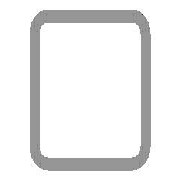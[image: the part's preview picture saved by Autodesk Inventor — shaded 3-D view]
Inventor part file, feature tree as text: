
AUTODESK INVENTOR PART (.ipt)
format: ipt  version: 2025 (Build 290162010, 162A)  size: 134,656 bytes
history: native  units: mm (DEFAULTED — no unit token found)
features: other x4, sketch x1, plane x1
ambient origin geometry x8: Origin, YZ Plane, XZ Plane, XY Plane, X Axis, Y Axis, Z Axis, Center Point
bodies: Solid1 (feature_tree), Body (feature_tree)
feature tree (6):
  parser-record x1  (decoder bookkeeping rows leaked as tree rows — omitted from the tree; the rows remain in map.json)
  other  "Driven Length"
  other  "Start Plane"
  other  "End Plane"
  sketch  "Sketch3"  dims[d3=650.0mm d4=0.0mm d7=4.0mm d9=40.0mm d11=40.0mm d12=2.0mm d13=40.0mm d14=690.0mm d15=20.0mm d16=20.0mm d17=90.0deg d18=650.0mm]
  plane  "Work Plane3"
